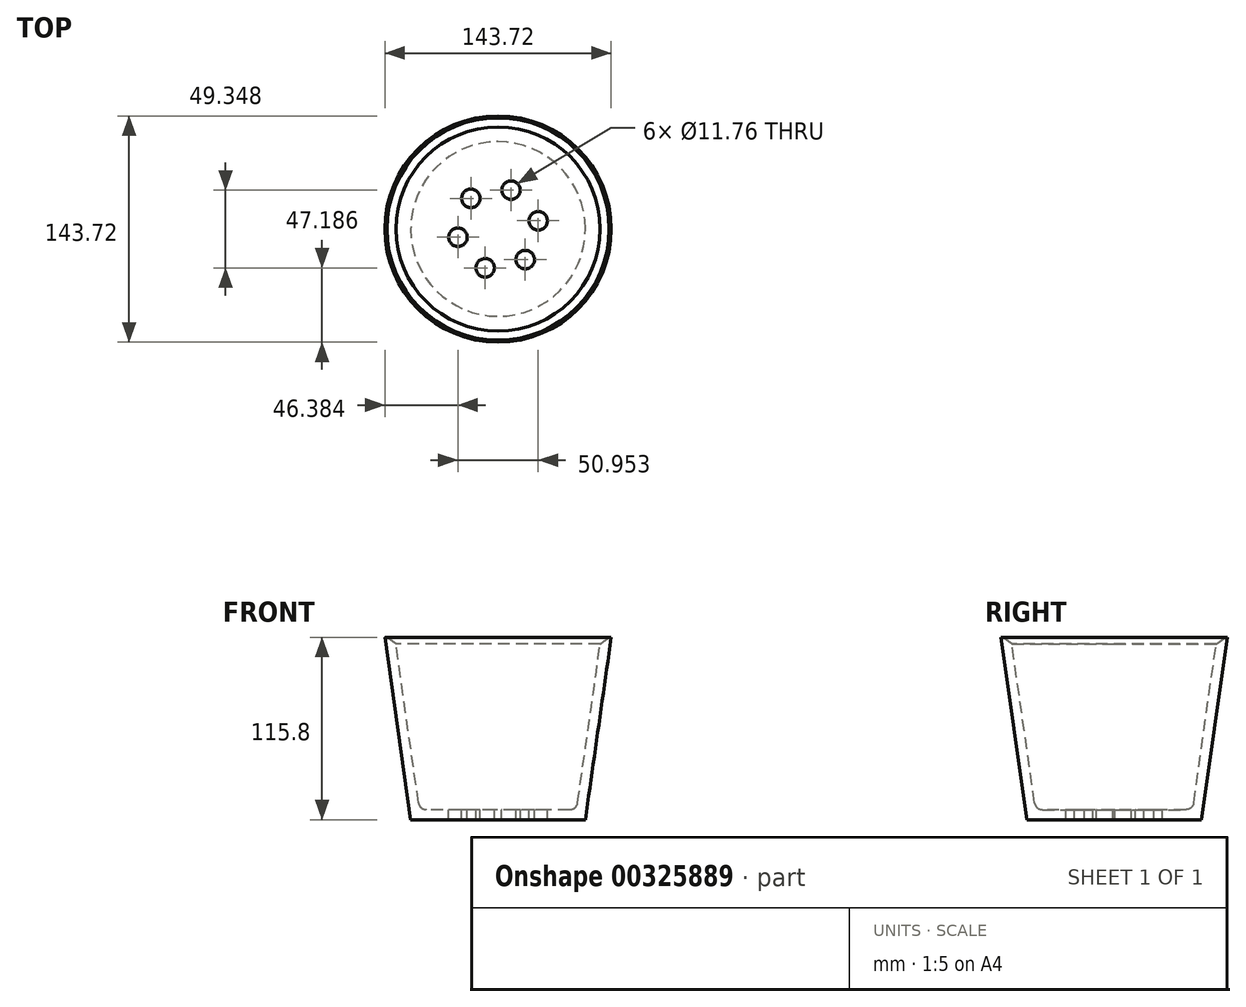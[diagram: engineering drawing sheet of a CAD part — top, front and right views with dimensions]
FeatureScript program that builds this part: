
annotation { "Feature Type Name" : "Feature", "Feature Type Description" : "" }
export const myFeature = defineFeature(function(context is Context, id is Id, definition is map)
    precondition{}
    {
        {
            var Q0;
            Q0=qCreatedBy(makeId("Front.planeOp"),FACE);
            var sketch = newSketch(context, id + "F0", { "sketchPlane" : qUnion([Q0])});
            skLineSegment(sketch, "E0", {"start": v(0, 0) * mm, "end": v(-55.45, 0) * mm});
            skLineSegment(sketch, "E1", {"start": v(-55.45, 0) * mm, "end": v(-71.86, 115.62) * mm});
            skLineSegment(sketch, "E2.0", {"start": v(-49.93, 6.35) * mm, "end": v(-65.58, 116.51) * mm});
            skLineSegment(sketch, "E2.1", {"start": v(0, 6.35) * mm, "end": v(-49.93, 6.35) * mm});
            skLineSegment(sketch, "E3", {"start": v(-71.86, 115.62) * mm, "end": v(-65.58, 116.51) * mm});
            skLineSegment(sketch, "E4", {"start": v(0, 6.35) * mm, "end": v(0, 0) * mm});
            skSolve(sketch);
        }
        {
            var Q0;
            Q0=makeQuery(id+"F0.imprint","IMPRINT",FACE,{"disambiguationData":[TD([[makeQuery(id+"F0.imprint","IMPRINT",EDGE,{"derivedFrom":sQuery(id+"F0.wireOp",EDGE,"E0")}),-1.0]])]});
            var Q1;
            Q1=sQuery(id+"F0.wireOp",EDGE,"E4");
            revolve(context, id + "F1", {"entities" : qUnion([Q0]), "axis" : qUnion([Q1]), "revolveType" : RevolveType.FULL});
        }
        {
            var Q0;
            Q0=makeQuery(id+"F1.opRevolve","SWEPT_EDGE",EDGE,{"disambiguationData":[OSD([sQuery(id+"F0.wireOp",EDGE,"E2.0"),sQuery(id+"F0.wireOp",EDGE,"E2.1")])]});
            fillet(context, id + "F2", {"entities" : qUnion([Q0]), "radius" : 5.08 * mm, "tangentPropagation" : true, "allowEdgeOverflow" : false});
        }
        {
            var Q0;
            Q0=makeQuery(id+"F1.opRevolve","SWEPT_EDGE",EDGE,{"disambiguationData":[OSD([sQuery(id+"F0.wireOp",EDGE,"E2.0"),sQuery(id+"F0.wireOp",EDGE,"E3")])]});
            chamfer(context, id + "F3", {"entities" : qUnion([Q0]), "width" : 5.08 * mm, "tangentPropagation" : true});
        }
        {
            var Q0;
            Q0=makeQuery(id+"F1.opRevolve","SWEPT_FACE",FACE,{"disambiguationData":[OSD([sQuery(id+"F0.wireOp",EDGE,"E2.1")])]});
            var sketch = newSketch(context, id + "F4", { "sketchPlane" : qUnion([Q0])});
            skCircle(sketch, "E5", {"center": v(0, 0) * mm, "radius": 26 * mm, "construction": true});
            skCircle(sketch, "E6", {"center": v(-17.26, 19.45) * mm, "radius": 5.88 * mm});
            skCircle(sketch, "E7.1.0", {"center": v(-25.48, -5.22) * mm, "radius": 5.88 * mm});
            skCircle(sketch, "E7.2.0", {"center": v(-8.22, -24.67) * mm, "radius": 5.88 * mm});
            skCircle(sketch, "E7.3.0", {"center": v(17.26, -19.45) * mm, "radius": 5.88 * mm});
            skCircle(sketch, "E7.4.0", {"center": v(25.48, 5.22) * mm, "radius": 5.88 * mm});
            skCircle(sketch, "E7.5.0", {"center": v(8.22, 24.67) * mm, "radius": 5.88 * mm});
            skSolve(sketch);
        }
        {
            var Q0;
            Q0=makeQuery(id+"F4.imprint","IMPRINT",FACE,{"disambiguationData":[TD([[makeQuery(id+"F4.imprint","IMPRINT",EDGE,{"derivedFrom":sQuery(id+"F4.wireOp",EDGE,"E6")}),1.0]])]});
            var Q1;
            Q1=makeQuery(id+"F4.imprint","IMPRINT",FACE,{"disambiguationData":[TD([[makeQuery(id+"F4.imprint","IMPRINT",EDGE,{"derivedFrom":sQuery(id+"F4.wireOp",EDGE,"E7.1.0")}),1.0]])]});
            var Q2;
            Q2=makeQuery(id+"F4.imprint","IMPRINT",FACE,{"disambiguationData":[TD([[makeQuery(id+"F4.imprint","IMPRINT",EDGE,{"derivedFrom":sQuery(id+"F4.wireOp",EDGE,"E7.2.0")}),1.0]])]});
            var Q3;
            Q3=makeQuery(id+"F4.imprint","IMPRINT",FACE,{"disambiguationData":[TD([[makeQuery(id+"F4.imprint","IMPRINT",EDGE,{"derivedFrom":sQuery(id+"F4.wireOp",EDGE,"E7.3.0")}),1.0]])]});
            var Q4;
            Q4=makeQuery(id+"F4.imprint","IMPRINT",FACE,{"disambiguationData":[TD([[makeQuery(id+"F4.imprint","IMPRINT",EDGE,{"derivedFrom":sQuery(id+"F4.wireOp",EDGE,"E7.4.0")}),1.0]])]});
            var Q5;
            Q5=makeQuery(id+"F4.imprint","IMPRINT",FACE,{"disambiguationData":[TD([[makeQuery(id+"F4.imprint","IMPRINT",EDGE,{"derivedFrom":sQuery(id+"F4.wireOp",EDGE,"E7.5.0")}),1.0]])]});
            extrude(context, id + "F5", {"entities" : qUnion([Q0, Q1, Q2, Q3, Q4, Q5]), "operationType" : NewBodyOperationType.REMOVE, "endBound" : BoundingType.THROUGH_ALL, "oppositeDirection" : true, "depth" : 25.4 * mm});
        }
    });
